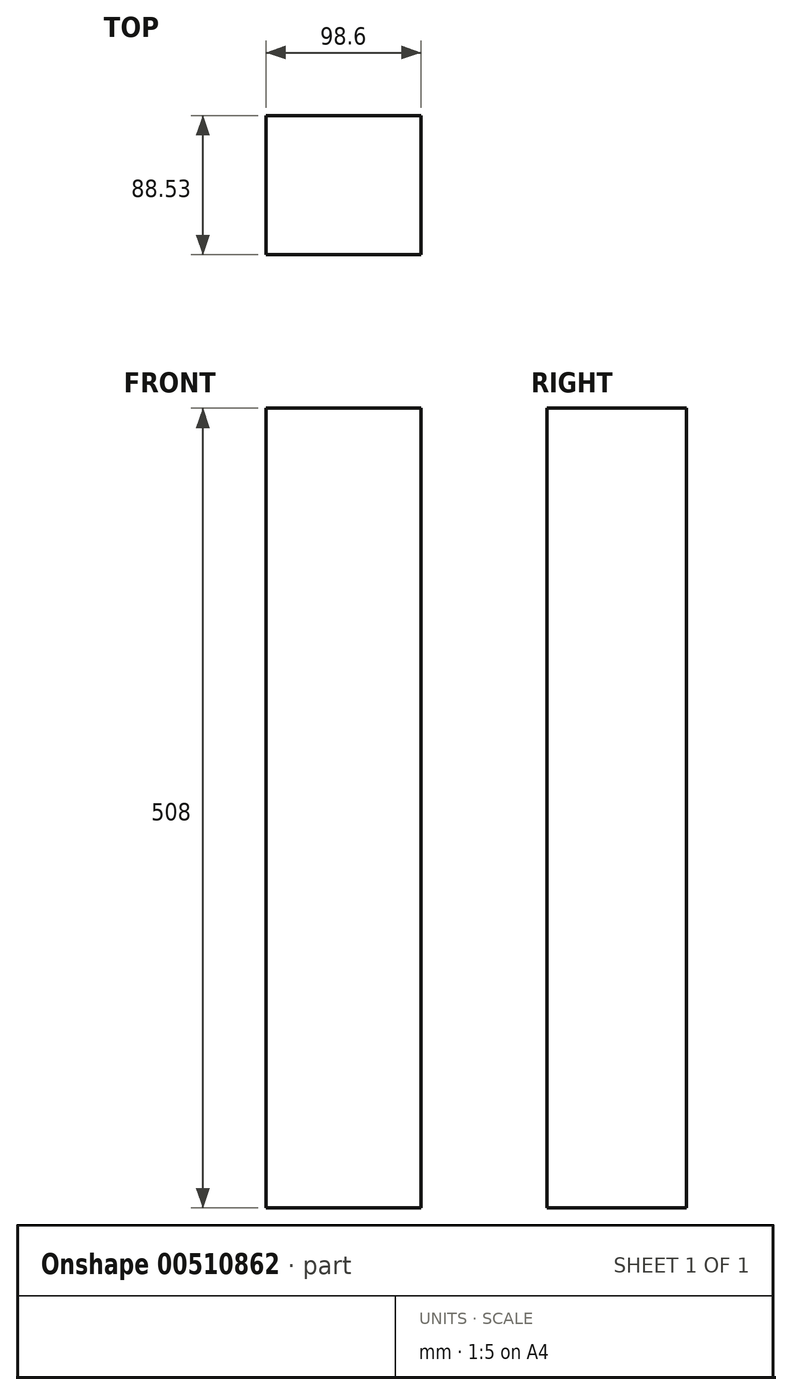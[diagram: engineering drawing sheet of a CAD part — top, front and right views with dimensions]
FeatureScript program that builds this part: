
annotation { "Feature Type Name" : "Feature", "Feature Type Description" : "" }
export const myFeature = defineFeature(function(context is Context, id is Id, definition is map)
    precondition{}
    {
        {
            var Q0;
            Q0=qCreatedBy(makeId("Top.planeOp"),FACE);
            var sketch = newSketch(context, id + "F0", { "sketchPlane" : qUnion([Q0])});
            skLineSegment(sketch, "E0.bottom", {"start": v(-46.4, 41.82) * mm, "end": v(52.2, 41.82) * mm});
            skLineSegment(sketch, "E0.top", {"start": v(-46.4, -46.7) * mm, "end": v(52.2, -46.7) * mm});
            skLineSegment(sketch, "E0.left", {"start": v(-46.4, 41.82) * mm, "end": v(-46.4, -46.7) * mm});
            skLineSegment(sketch, "E0.right", {"start": v(52.2, 41.82) * mm, "end": v(52.2, -46.7) * mm});
            skSolve(sketch);
        }
        {
            var Q0;
            Q0=makeQuery(id+"F0.imprint","IMPRINT",FACE,{"disambiguationData":[TD([[makeQuery(id+"F0.imprint","IMPRINT",EDGE,{"derivedFrom":sQuery(id+"F0.wireOp",EDGE,"E0.bottom")}),-1.0]])]});
            extrude(context, id + "F1", {"entities" : qUnion([Q0]), "depth" : 508 * mm});
        }
    });
